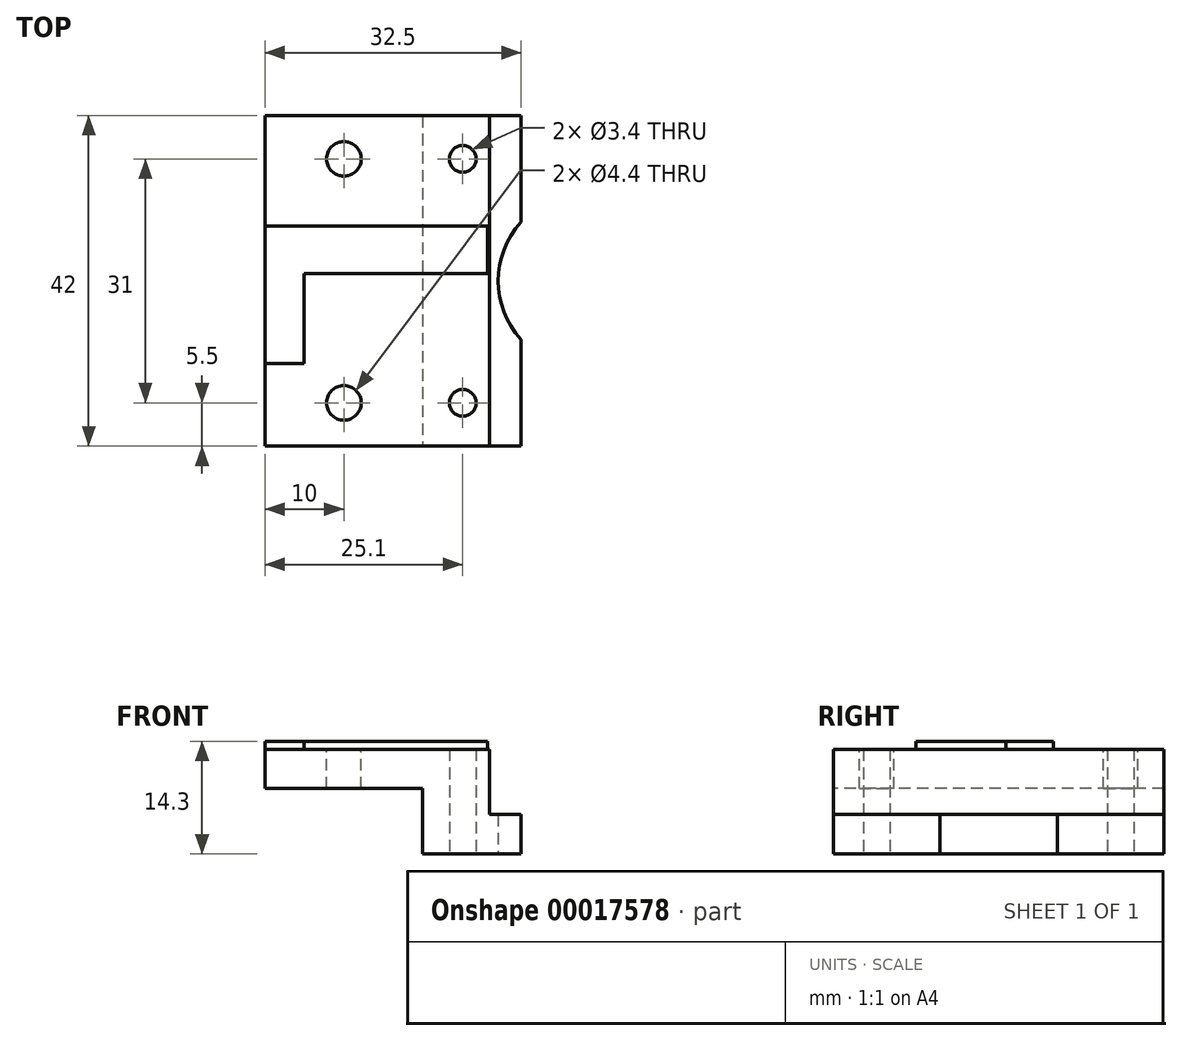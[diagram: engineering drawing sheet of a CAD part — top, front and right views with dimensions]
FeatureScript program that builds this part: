
annotation { "Feature Type Name" : "Feature", "Feature Type Description" : "" }
export const myFeature = defineFeature(function(context is Context, id is Id, definition is map)
    precondition{}
    {
        {
            var Q0;
            Q0=qCreatedBy(makeId("Front.planeOp"),FACE);
            var sketch = newSketch(context, id + "F0", { "sketchPlane" : qUnion([Q0])});
            skLineSegment(sketch, "E0", {"start": v(8.5, 13.3) * mm, "end": v(8.5, 5) * mm});
            skLineSegment(sketch, "E1", {"start": v(8.5, 5) * mm, "end": v(12.5, 5) * mm});
            skLineSegment(sketch, "E2", {"start": v(12.5, 5) * mm, "end": v(12.5, 0) * mm});
            skLineSegment(sketch, "E3", {"start": v(12.5, 0) * mm, "end": v(0, 0) * mm});
            skLineSegment(sketch, "E4", {"start": v(0, 0) * mm, "end": v(0, 13.3) * mm});
            skLineSegment(sketch, "E5", {"start": v(0, 13.3) * mm, "end": v(8.5, 13.3) * mm});
            skSolve(sketch);
        }
        {
            var Q0;
            Q0=qSketchRegion(id+"F0",true);
            extrude(context, id + "F1", {"entities" : qUnion([Q0]), "oppositeDirection" : true, "depth" : 42 * mm});
        }
        {
            var Q0;
            Q0=makeQuery(id+"F1.opExtrude","SWEPT_FACE",FACE,{"disambiguationData":[OSD([sQuery(id+"F0.wireOp",EDGE,"E3")])]});
            var sketch = newSketch(context, id + "F2", { "sketchPlane" : qUnion([Q0])});
            skCircle(sketch, "E6", {"center": v(5.1, -5.5) * mm, "radius": 1.7 * mm});
            skCircle(sketch, "E7", {"center": v(5.1, -36.5) * mm, "radius": 1.7 * mm});
            skCircle(sketch, "E8", {"center": v(20.6, -21) * mm, "radius": 11 * mm});
            skLineSegment(sketch, "E9", {"start": v(0, -21) * mm, "end": v(12.5, -21) * mm, "construction": true});
            skSolve(sketch);
        }
        {
            var Q0;
            Q0=qSketchRegion(id+"F2",true);
            extrude(context, id + "F3", {"entities" : qUnion([Q0]), "operationType" : NewBodyOperationType.REMOVE, "endBound" : BoundingType.THROUGH_ALL, "oppositeDirection" : true, "depth" : 25 * mm});
        }
        {
            var Q0;
            Q0=makeQuery(id+"F1.opExtrude","SWEPT_FACE",FACE,{"disambiguationData":[OSD([sQuery(id+"F0.wireOp",EDGE,"E4")])]});
            var sketch = newSketch(context, id + "F4", { "sketchPlane" : qUnion([Q0])});
            skLineSegment(sketch, "E10.bottom", {"start": v(-42, 13.3) * mm, "end": v(0, 13.3) * mm});
            skLineSegment(sketch, "E10.top", {"start": v(-42, 8.3) * mm, "end": v(0, 8.3) * mm});
            skLineSegment(sketch, "E10.left", {"start": v(-42, 13.3) * mm, "end": v(-42, 8.3) * mm});
            skLineSegment(sketch, "E10.right", {"start": v(0, 13.3) * mm, "end": v(0, 8.3) * mm});
            skSolve(sketch);
        }
        {
            var Q0;
            Q0=qSketchRegion(id+"F4",true);
            extrude(context, id + "F5", {"entities" : qUnion([Q0]), "operationType" : NewBodyOperationType.ADD, "depth" : 20 * mm});
        }
        {
            var Q0;
            Q0=makeQuery(id+"F5.boolean.opBoolean","MERGE",FACE,{"derivedFrom":[makeQuery(id+"F1.opExtrude","SWEPT_FACE",FACE,{"disambiguationData":[OSD([sQuery(id+"F0.wireOp",EDGE,"E5")])]}),makeQuery(id+"F5.opExtrude","SWEPT_FACE",FACE,{"disambiguationData":[OSD([sQuery(id+"F4.wireOp",EDGE,"E10.bottom")])]})]});
            var sketch = newSketch(context, id + "F6", { "sketchPlane" : qUnion([Q0])});
            skCircle(sketch, "E11", {"center": v(-10, 36.5) * mm, "radius": 2.2 * mm});
            skCircle(sketch, "E12", {"center": v(-10, 5.5) * mm, "radius": 2.2 * mm});
            skPoint(sketch, "E13", {"position": v(5.1, 36.5) * mm});
            skPoint(sketch, "E14", {"position": v(5.1, 5.5) * mm});
            skSolve(sketch);
        }
        {
            var Q0;
            Q0=qSketchRegion(id+"F6",true);
            extrude(context, id + "F7", {"entities" : qUnion([Q0]), "operationType" : NewBodyOperationType.REMOVE, "oppositeDirection" : true, "depth" : 25 * mm});
        }
        {
            var Q0;
            Q0=makeQuery(id+"F5.boolean.opBoolean","MERGE",FACE,{"derivedFrom":[makeQuery(id+"F1.opExtrude","SWEPT_FACE",FACE,{"disambiguationData":[OSD([sQuery(id+"F0.wireOp",EDGE,"E5")])]}),makeQuery(id+"F5.opExtrude","SWEPT_FACE",FACE,{"disambiguationData":[OSD([sQuery(id+"F4.wireOp",EDGE,"E10.bottom")])]})]});
            var sketch = newSketch(context, id + "F8", { "sketchPlane" : qUnion([Q0])});
            skText(sketch, "E15", { "text": "L", "fontName": "OpenSans-Bold.ttf"});
            const initialGuessF8  = {"E15": [-0.02, 0.0315, 0, -1, 0.0285]};
            skSetInitialGuess(sketch, initialGuessF8);
            skSolve(sketch);
        }
        {
            var Q0;
            Q0=qSketchRegion(id+"F8",true);
            extrude(context, id + "F9", {"entities" : qUnion([Q0]), "operationType" : NewBodyOperationType.ADD, "depth" : 1 * mm});
        }
    });
